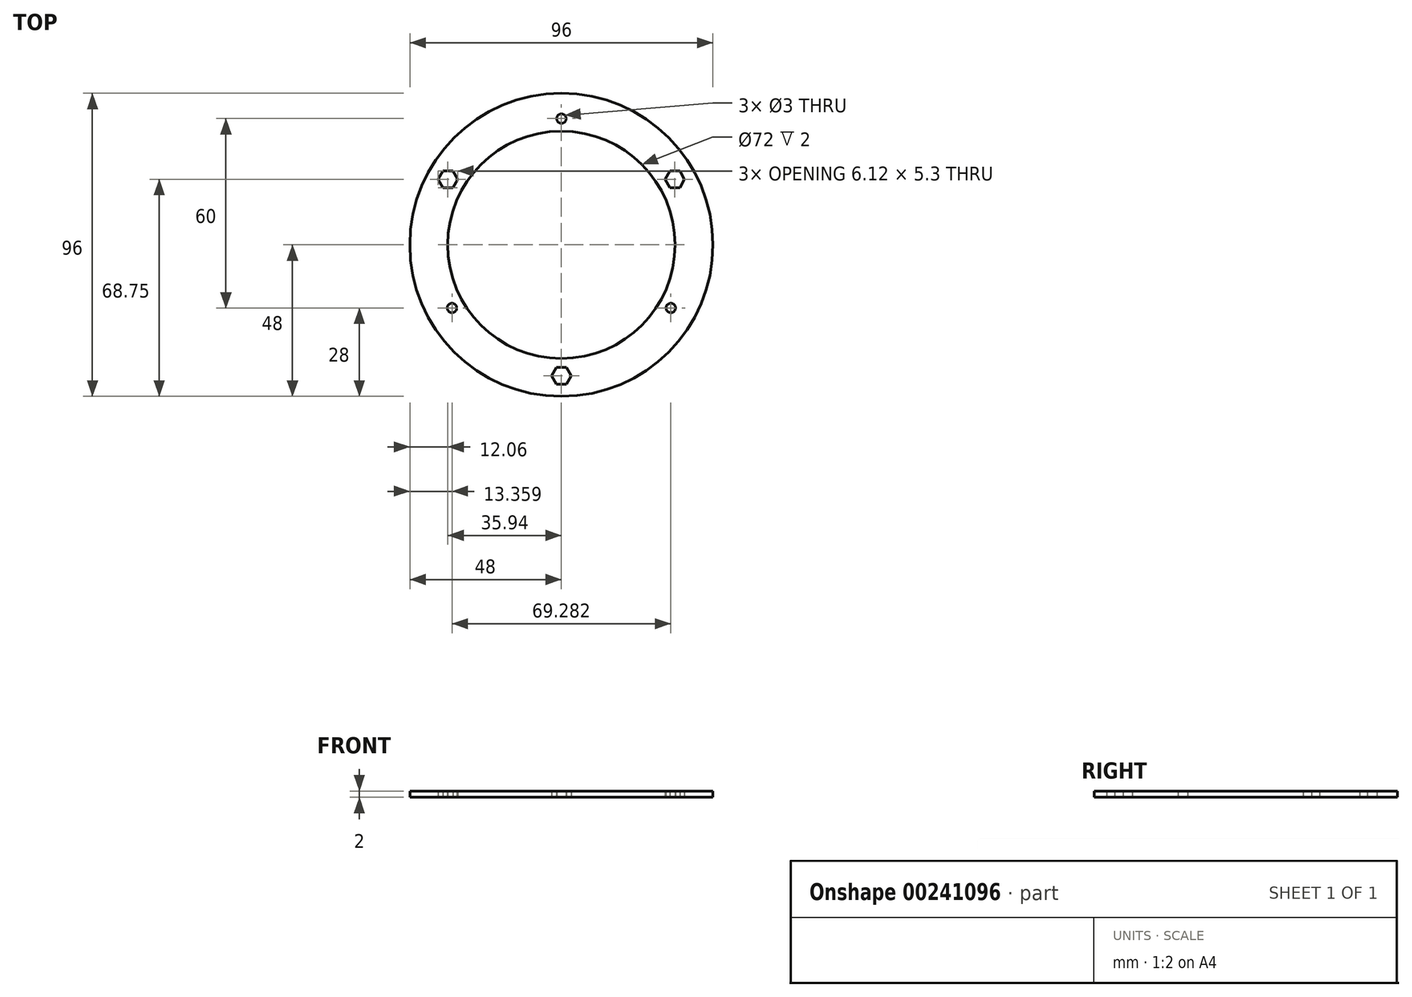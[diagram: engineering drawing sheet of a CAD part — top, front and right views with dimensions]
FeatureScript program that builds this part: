
annotation { "Feature Type Name" : "Feature", "Feature Type Description" : "" }
export const myFeature = defineFeature(function(context is Context, id is Id, definition is map)
    precondition{}
    {
        {
            var Q0;
            Q0=qCreatedBy(makeId("Top.planeOp"),FACE);
            var sketch = newSketch(context, id + "F0", { "sketchPlane" : qUnion([Q0])});
            skCircle(sketch, "E0", {"center": v(0, 0) * mm, "radius": 48 * mm});
            skCircle(sketch, "E1", {"center": v(0, 0) * mm, "radius": 36 * mm});
            skCircle(sketch, "E2", {"center": v(0, 40) * mm, "radius": 1.5 * mm});
            skCircle(sketch, "E3.1.0", {"center": v(-34.64, -20) * mm, "radius": 1.5 * mm});
            skCircle(sketch, "E3.2.0", {"center": v(34.64, -20) * mm, "radius": 1.5 * mm});
            skCircle(sketch, "E4.cCircle", {"center": v(0, -41.5) * mm, "radius": 2.65 * mm, "construction": true});
            skLineSegment(sketch, "E4.0", {"start": v(-1.53, -38.85) * mm, "end": v(1.53, -38.85) * mm});
            skLineSegment(sketch, "E4.1", {"start": v(1.53, -38.85) * mm, "end": v(3.06, -41.5) * mm});
            skLineSegment(sketch, "E4.2", {"start": v(3.06, -41.5) * mm, "end": v(1.53, -44.15) * mm});
            skLineSegment(sketch, "E4.3", {"start": v(1.53, -44.15) * mm, "end": v(-1.53, -44.15) * mm});
            skLineSegment(sketch, "E4.4", {"start": v(-1.53, -44.15) * mm, "end": v(-3.06, -41.5) * mm});
            skLineSegment(sketch, "E4.5", {"start": v(-3.06, -41.5) * mm, "end": v(-1.53, -38.85) * mm});
            skPoint(sketch, "E4.0.midPoint", {"position": v(0, -38.85) * mm});
            skLineSegment(sketch, "E5.1.0", {"start": v(32.88, 20.75) * mm, "end": v(34.41, 23.4) * mm});
            skLineSegment(sketch, "E5.1.1", {"start": v(34.41, 18.1) * mm, "end": v(32.88, 20.75) * mm});
            skLineSegment(sketch, "E5.1.2", {"start": v(37.47, 18.1) * mm, "end": v(34.41, 18.1) * mm});
            skCircle(sketch, "E5.1.3", {"center": v(35.94, 20.75) * mm, "radius": 2.65 * mm, "construction": true});
            skLineSegment(sketch, "E5.1.4", {"start": v(39, 20.75) * mm, "end": v(37.47, 18.1) * mm});
            skLineSegment(sketch, "E5.1.5", {"start": v(37.47, 23.4) * mm, "end": v(39, 20.75) * mm});
            skLineSegment(sketch, "E5.1.6", {"start": v(34.41, 23.4) * mm, "end": v(37.47, 23.4) * mm});
            skLineSegment(sketch, "E5.2.0", {"start": v(-34.41, 18.1) * mm, "end": v(-37.47, 18.1) * mm});
            skLineSegment(sketch, "E5.2.1", {"start": v(-32.88, 20.75) * mm, "end": v(-34.41, 18.1) * mm});
            skLineSegment(sketch, "E5.2.2", {"start": v(-34.41, 23.4) * mm, "end": v(-32.88, 20.75) * mm});
            skCircle(sketch, "E5.2.3", {"center": v(-35.94, 20.75) * mm, "radius": 2.65 * mm, "construction": true});
            skLineSegment(sketch, "E5.2.4", {"start": v(-37.47, 23.4) * mm, "end": v(-34.41, 23.4) * mm});
            skLineSegment(sketch, "E5.2.5", {"start": v(-39, 20.75) * mm, "end": v(-37.47, 23.4) * mm});
            skLineSegment(sketch, "E5.2.6", {"start": v(-37.47, 18.1) * mm, "end": v(-39, 20.75) * mm});
            skSolve(sketch);
        }
        {
            var Q0;
            Q0=qSketchRegion(id+"F0",true);
            extrude(context, id + "F1", {"entities" : qUnion([Q0]), "depth" : 2 * mm});
        }
    });
